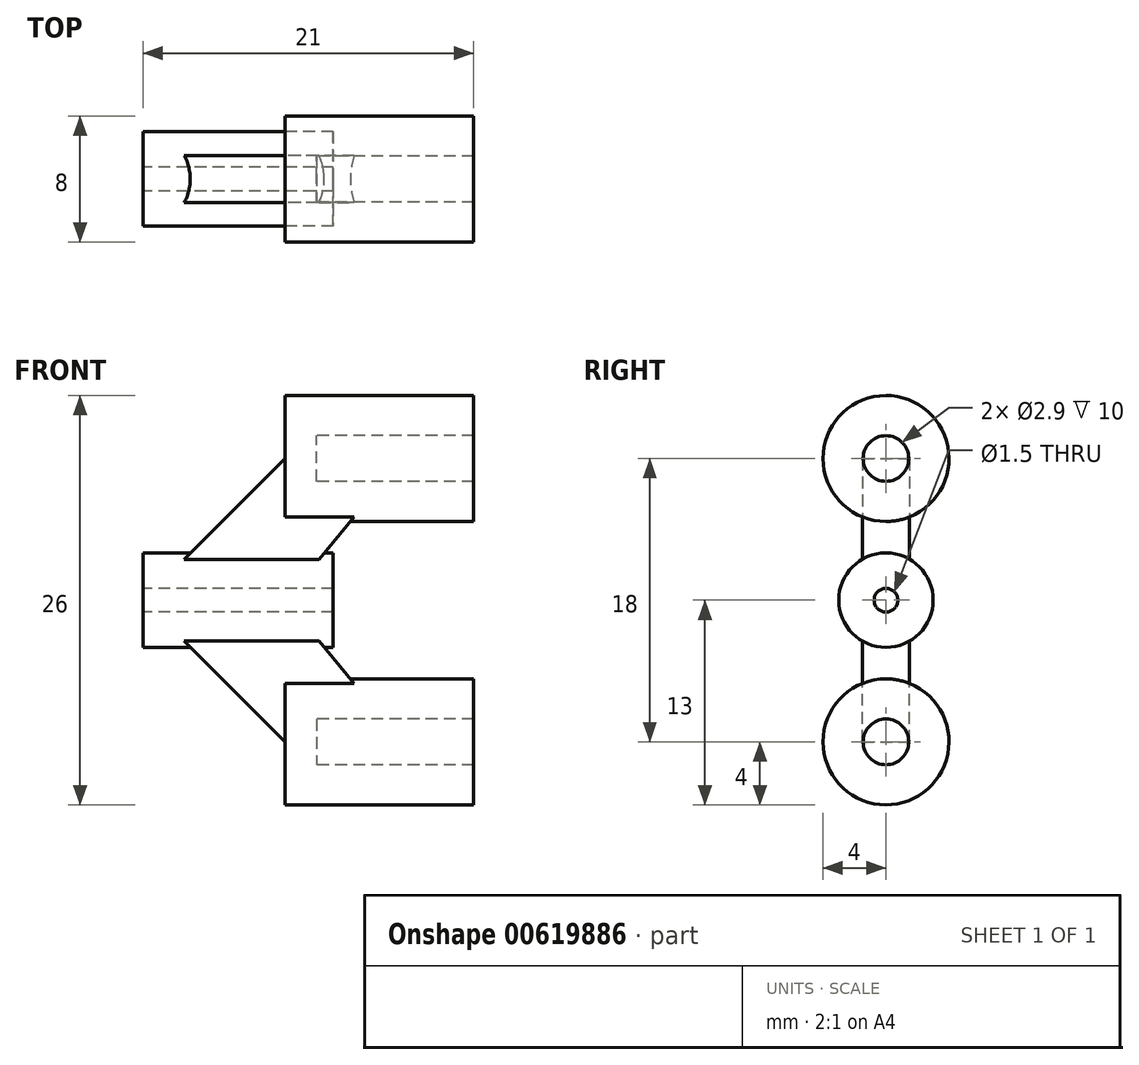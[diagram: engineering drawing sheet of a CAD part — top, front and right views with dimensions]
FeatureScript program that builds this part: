
annotation { "Feature Type Name" : "Feature", "Feature Type Description" : "" }
export const myFeature = defineFeature(function(context is Context, id is Id, definition is map)
    precondition{}
    {
        {
            var Q0;
            Q0=qCreatedBy(makeId("Right.planeOp"),FACE);
            var sketch = newSketch(context, id + "F0", { "sketchPlane" : qUnion([Q0])});
            skCircle(sketch, "E0", {"center": v(0, 0) * mm, "radius": 4 * mm});
            skSolve(sketch);
        }
        {
            var Q0;
            Q0=qSketchRegion(id+"F0",true);
            extrude(context, id + "F1", {"entities" : qUnion([Q0]), "depth" : 2 * mm, "offsetDistance" : 25 * mm});
        }
        {
            var Q0;
            Q0=makeQuery(id+"F1.opExtrude","CAP_FACE",FACE,{"disambiguationData":[OSD([sQuery(id+"F0.wireOp",EDGE,"E0")])],"isStart":false});
            var sketch = newSketch(context, id + "F2", { "sketchPlane" : qUnion([Q0])});
            skCircle(sketch, "E1", {"center": v(0, 0) * mm, "radius": 1.45 * mm});
            skCircle(sketch, "E2.0", {"center": v(0, 0) * mm, "radius": 4 * mm});
            skSolve(sketch);
        }
        {
            var Q0;
            Q0=qSketchRegion(id+"F2",true);
            extrude(context, id + "F3", {"entities" : qUnion([Q0]), "operationType" : NewBodyOperationType.ADD, "depth" : 10 * mm, "offsetDistance" : 25 * mm});
        }
        {
            var Q0;
            Q0=qCreatedBy(makeId("Front.planeOp"),FACE);
            var sketch = newSketch(context, id + "F4", { "sketchPlane" : qUnion([Q0])});
            skLineSegment(sketch, "E3", {"start": v(0, 0) * mm, "end": v(-9, -9) * mm});
            skLineSegment(sketch, "E4", {"start": v(-9, -9) * mm, "end": v(0, -9) * mm});
            skLineSegment(sketch, "E5", {"start": v(0, -9) * mm, "end": v(5, -3) * mm});
            skLineSegment(sketch, "E6", {"start": v(0, 0) * mm, "end": v(0, -3) * mm});
            skLineSegment(sketch, "E7", {"start": v(0, -3) * mm, "end": v(5, -3) * mm});
            skSolve(sketch);
        }
        {
            var Q0;
            Q0=qSketchRegion(id+"F4",true);
            extrude(context, id + "F5", {"entities" : qUnion([Q0]), "operationType" : NewBodyOperationType.ADD, "endBound" : BoundingType.SYMMETRIC, "depth" : 3 * mm, "offsetDistance" : 25 * mm});
        }
        {
            var Q0;
            Q0=makeQuery(id+"F5.opExtrude","SWEPT_EDGE",EDGE,{"disambiguationData":[OSD([sQuery(id+"F4.wireOp",EDGE,"E3"),sQuery(id+"F4.wireOp",EDGE,"E4")])]});
            cPoint(context, id + "F6", {"entities" : qUnion([Q0]), "parameter" : 0.5});
        }
        {
            var Q0;
            Q0=qCreatedBy(id+"F6",VERTEX);
            var Q1;
            Q1=qCreatedBy(makeId("Right.planeOp"),FACE);
            cPlane(context, id + "F7", {"entities" : qUnion([Q0, Q1]), "cplaneType" : CPlaneType.PLANE_POINT, "offset" : 25 * mm, "width" : 150 * mm, "height" : 150 * mm});
        }
        {
            var Q0;
            Q0=qCreatedBy(id+"F7.planeOp",FACE);
            var sketch = newSketch(context, id + "F8", { "sketchPlane" : qUnion([Q0])});
            skPoint(sketch, "E8.0", {"position": v(0, -9) * mm});
            skCircle(sketch, "E9", {"center": v(0, -9) * mm, "radius": 0.65 * mm, "construction": true});
            skCircle(sketch, "E10", {"center": v(0, -9) * mm, "radius": 3 * mm});
            skSolve(sketch);
        }
        {
            var Q0;
            Q0=qSketchRegion(id+"F8",true);
            extrude(context, id + "F9", {"entities" : qUnion([Q0]), "operationType" : NewBodyOperationType.ADD, "depth" : 12.07 * mm, "offsetDistance" : 25 * mm});
        }
        {
            var Q0;
            Q0=makeQuery(id+"F9.opExtrude","CAP_FACE",FACE,{"disambiguationData":[OSD([sQuery(id+"F8.wireOp",EDGE,"E10")])],"isStart":true});
            var sketch = newSketch(context, id + "F10", { "sketchPlane" : qUnion([Q0])});
            skCircle(sketch, "E11", {"center": v(0, -9) * mm, "radius": 0.75 * mm});
            skSolve(sketch);
        }
        {
            var Q0;
            Q0=qSketchRegion(id+"F10",true);
            extrude(context, id + "F11", {"entities" : qUnion([Q0]), "operationType" : NewBodyOperationType.REMOVE, "oppositeDirection" : true, "depth" : 25 * mm, "offsetDistance" : 25 * mm});
        }
        {
            var Q0;
            Q0=qCreatedBy(makeId("Top.planeOp"),FACE);
            cPlane(context, id + "F12", {"entities" : qUnion([Q0]), "cplaneType" : CPlaneType.OFFSET, "offset" : 9 * mm, "oppositeDirection" : true, "width" : 150 * mm, "height" : 150 * mm});
        }
        {
            var Q0;
            Q0=makeQuery(id+"F1.opExtrude","SWEPT_BODY",BODY,{"disambiguationData":[OSD([sQuery(id+"F0.wireOp",EDGE,"E0")])]});
            var Q1;
            Q1=qCreatedBy(id+"F12.planeOp",FACE);
            mirror(context, id + "F13", {"operationType" : NewBodyOperationType.ADD, "entities" : qUnion([Q0]), "mirrorPlane" : qUnion([Q1])});
        }
    });
